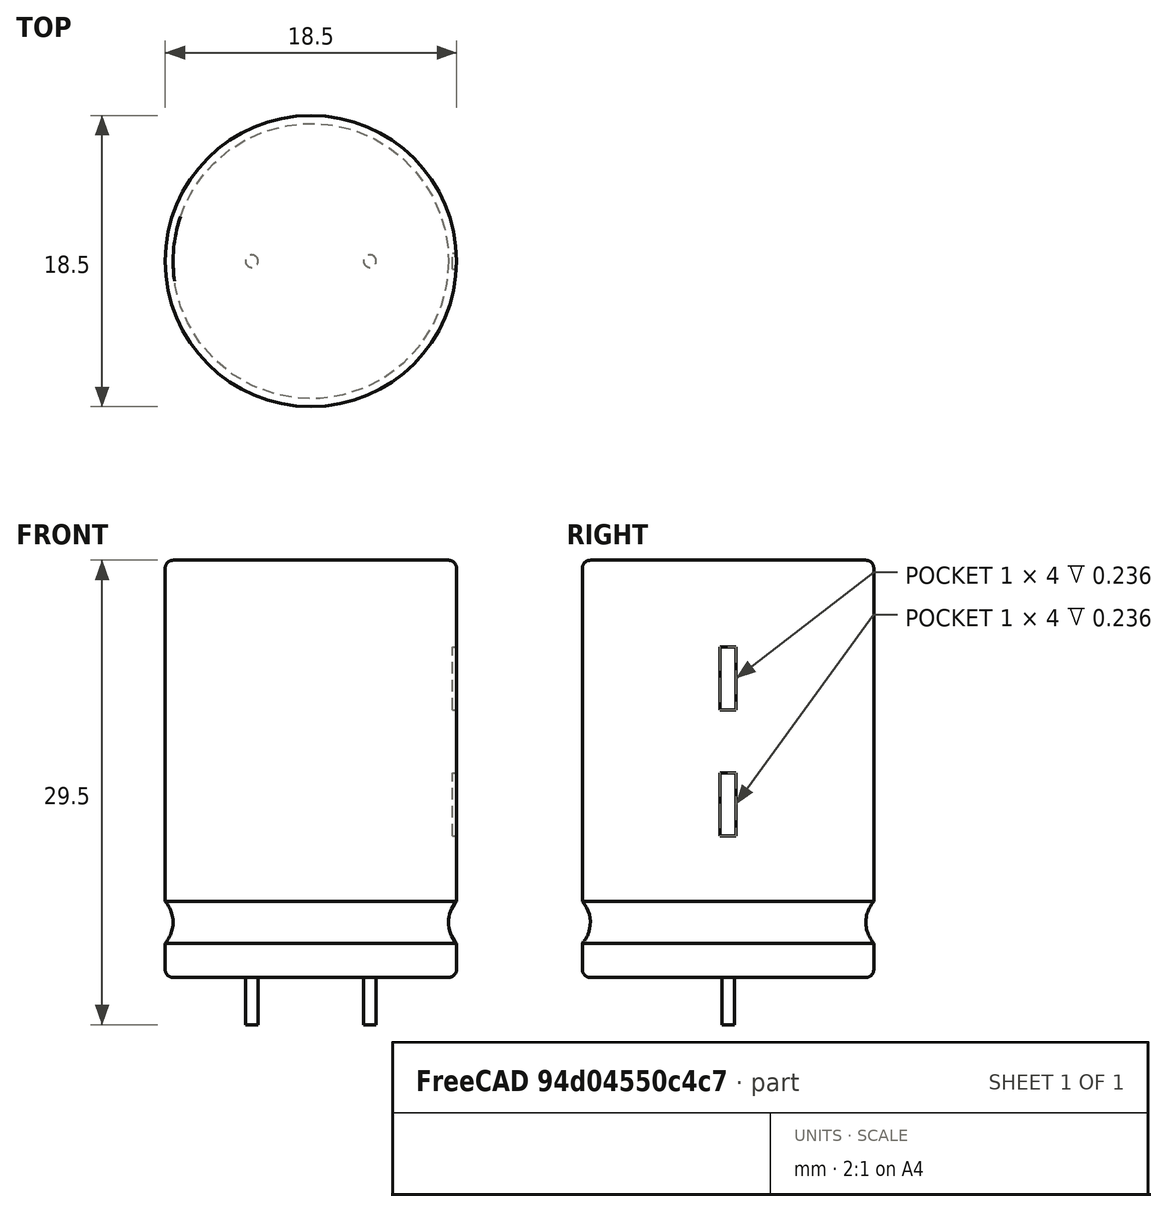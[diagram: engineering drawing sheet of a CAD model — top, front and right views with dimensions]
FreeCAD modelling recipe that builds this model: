
FCSTD DOCUMENT
Label: CAPPR750W80D1800H2500
objects: Part::Cylinder×3, Part::Cut×3, Part::Box×2, Part::Fuse×2, Part::Fillet×1, Part::Torus×1
note: 12 computed .brp shape members not serialized (recipe doc carries the construction recipe); baked Part::Feature solids carry a one-line shape summary decoded from their .brp

FEATURE [Part::Cylinder] Cylinder  label="Grundkoerper"
  Angle = 360
  Height = 26.5
  Radius = 9.25
FEATURE [Part::Cylinder] Cylinder001  label="Pin1+"
  Angle = 360
  Height = 3
  Placement = pos=(-3.75,0,-3) rot=(0,0,1;0rad)
  Radius = 0.4
FEATURE [Part::Cylinder] Cylinder002  label="Pin2-"
  Angle = 360
  Height = 3
  Placement = pos=(3.75,0,-3) rot=(0,0,1;0rad)
  Radius = 0.4
FEATURE [Part::Fillet] Fillet  label="Abgerundeter Grundkoerper"
  Base = -> Cylinder
  Edges = 2 edges r=0.5: [Edge1,Edge3]
FEATURE [Part::Torus] Torus  label="Ring"
  Angle1 = -180
  Angle2 = 180
  Angle3 = 360
  Placement = pos=(0,0,3.5) rot=(0,0,1;0rad)
  Radius1 = 10.75
  Radius2 = 2
FEATURE [Part::Cut] Cut  label="Beringter kondensator"
  Base = -> Fillet
  Tool = -> Torus
FEATURE [Part::Box] Box
  Height = 4
  Length = 1
  Placement = pos=(9,-0.5,9) rot=(0,0,1;0rad)
  Width = 1
FEATURE [Part::Box] Box001
  Height = 4
  Length = 1
  Placement = pos=(9,-0.5,17) rot=(0,0,1;0rad)
  Width = 1
FEATURE [Part::Cut] Cut001
  Base = -> Cut
  Tool = -> Box
FEATURE [Part::Cut] Cut002
  Base = -> Cut001
  Tool = -> Box001
FEATURE [Part::Fuse] Fusion
  Base = -> Cut002
  Tool = -> Cylinder001
FEATURE [Part::Fuse] Fusion001  label="CAPPR750W80D1800H2500"
  Base = -> Fusion
  Tool = -> Cylinder002
